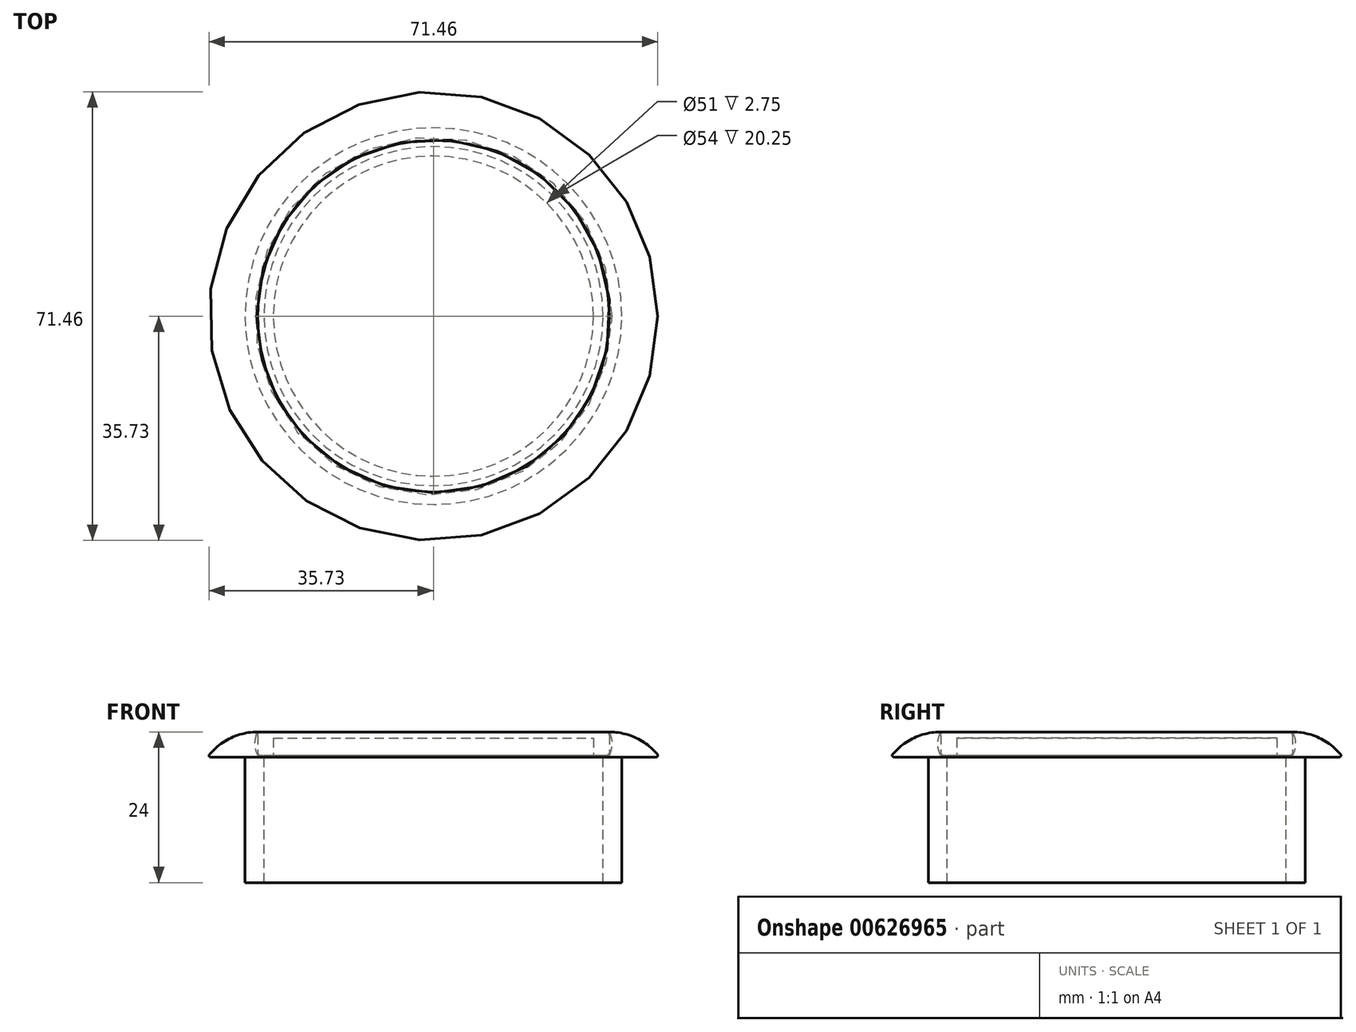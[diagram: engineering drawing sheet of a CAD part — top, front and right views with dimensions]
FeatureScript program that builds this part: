
annotation { "Feature Type Name" : "Feature", "Feature Type Description" : "" }
export const myFeature = defineFeature(function(context is Context, id is Id, definition is map)
    precondition{}
    {
        {
            var Q0;
            Q0=qCreatedBy(makeId("Top.planeOp"),FACE);
            var sketch = newSketch(context, id + "F0", { "sketchPlane" : qUnion([Q0])});
            skCircle(sketch, "E0", {"center": v(0, 0) * mm, "radius": 27 * mm});
            skCircle(sketch, "E1", {"center": v(0, 0) * mm, "radius": 30 * mm});
            skSolve(sketch);
        }
        {
            var Q0;
            Q0=makeQuery(id+"F0.imprint","IMPRINT",FACE,{"disambiguationData":[TD([[makeQuery(id+"F0.imprint","IMPRINT",EDGE,{"derivedFrom":sQuery(id+"F0.wireOp",EDGE,"E0")}),-1.0]])]});
            extrude(context, id + "F1", {"entities" : qUnion([Q0]), "oppositeDirection" : true, "depth" : 20 * mm, "offsetDistance" : 25 * mm});
        }
        {
            var Q0;
            Q0=qCreatedBy(makeId("Front.planeOp"),FACE);
            var sketch = newSketch(context, id + "F2", { "sketchPlane" : qUnion([Q0])});
            skPoint(sketch, "E2", {"position": v(-27, 0) * mm});
            skPoint(sketch, "E3", {"position": v(-30, 0) * mm});
            skLineSegment(sketch, "E4", {"start": v(-27, 0) * mm, "end": v(-27, 0.25) * mm});
            skLineSegment(sketch, "E5", {"start": v(-27, 0.25) * mm, "end": v(-28, 0.25) * mm});
            skLineSegment(sketch, "E6", {"start": v(-28, 0.25) * mm, "end": v(-28, 4) * mm});
            skLineSegment(sketch, "E7", {"start": v(-30, 0) * mm, "end": v(-36, 0) * mm});
            skLineSegment(sketch, "E8", {"start": v(-28, 4) * mm, "end": v(0, 4) * mm});
            skLineSegment(sketch, "E9", {"start": v(0, 4) * mm, "end": v(0, 0) * mm, "construction": true});
            skArc(sketch, "E10", {"start": v(-28, 4) * mm, "mid": v(-32.47, 2.94) * mm, "end": v(-36, 0) * mm});
            skLineSegment(sketch, "E11", {"start": v(-30, 0) * mm, "end": v(-27, 0) * mm});
            skArc(sketch, "E12", {"start": v(-28, 4) * mm, "mid": v(-28.47, 2.13) * mm, "end": v(-28, 0.25) * mm});
            skLineSegment(sketch, "E13", {"start": v(-27, 0.25) * mm, "end": v(0, 0.25) * mm});
            skLineSegment(sketch, "E14", {"start": v(0, 0.25) * mm, "end": v(0, 4) * mm});
            skSolve(sketch);
        }
        {
            var Q0;
            Q0=makeQuery(id+"F2.imprint","IMPRINT",FACE,{"disambiguationData":[TD([[makeQuery(id+"F2.imprint","IMPRINT",EDGE,{"derivedFrom":sQuery(id+"F2.wireOp",EDGE,"E4")}),1.0]])]});
            var Q1;
            Q1=sQuery(id+"F2.wireOp",EDGE,"E9");
            revolve(context, id + "F3", {"operationType" : NewBodyOperationType.ADD, "entities" : qUnion([Q0]), "axis" : qUnion([Q1]), "revolveType" : RevolveType.FULL});
        }
        {
            var Q0;
            Q0=makeQuery(id+"F3.opRevolve","SWEPT_EDGE",EDGE,{"disambiguationData":[OSD([sQuery(id+"F2.wireOp",EDGE,"E8"),sQuery(id+"F2.wireOp",EDGE,"E10"),sQuery(id+"F2.wireOp",EDGE,"E12")])]});
            var Q1;
            Q1=makeQuery(id+"F3.opRevolve","SWEPT_EDGE",EDGE,{"disambiguationData":[OSD([sQuery(id+"F2.wireOp",EDGE,"E7"),sQuery(id+"F2.wireOp",EDGE,"E10")])]});
            fillet(context, id + "F4", {"entities" : qUnion([Q0, Q1]), "radius" : 0.25 * mm, "tangentPropagation" : true, "allowEdgeOverflow" : false});
        }
        {
            var Q0;
            Q0=makeQuery(id+"F2.imprint","IMPRINT",FACE,{"disambiguationData":[TD([[makeQuery(id+"F2.imprint","IMPRINT",EDGE,{"derivedFrom":sQuery(id+"F2.wireOp",EDGE,"E5")}),-1.0]])]});
            var Q1;
            Q1=sQuery(id+"F2.wireOp",EDGE,"E14");
            revolve(context, id + "F5", {"entities" : qUnion([Q0]), "axis" : qUnion([Q1]), "revolveType" : RevolveType.FULL});
        }
        {
            var Q0;
            Q0=makeQuery(id+"F5.opRevolve","SWEPT_EDGE",EDGE,{"disambiguationData":[OSD([sQuery(id+"F2.wireOp",EDGE,"E8"),sQuery(id+"F2.wireOp",EDGE,"E10"),sQuery(id+"F2.wireOp",EDGE,"E12")])]});
            var Q1;
            Q1=makeQuery(id+"F5.opRevolve","SWEPT_EDGE",EDGE,{"disambiguationData":[OSD([sQuery(id+"F2.wireOp",EDGE,"E5"),sQuery(id+"F2.wireOp",EDGE,"E6"),sQuery(id+"F2.wireOp",EDGE,"E12")])]});
            fillet(context, id + "F6", {"entities" : qUnion([Q0, Q1]), "radius" : 0.5 * mm, "tangentPropagation" : true, "allowEdgeOverflow" : false});
        }
        {
            var Q0;
            Q0=makeQuery(id+"F5.opRevolve","SWEPT_FACE",FACE,{"disambiguationData":[OSD([sQuery(id+"F2.wireOp",EDGE,"E5"),sQuery(id+"F2.wireOp",EDGE,"E13")])]});
            var sketch = newSketch(context, id + "F7", { "sketchPlane" : qUnion([Q0])});
            skCircle(sketch, "E15", {"center": v(0, 0) * mm, "radius": 25.5 * mm});
            skSolve(sketch);
        }
        {
            var Q0;
            Q0=makeQuery(id+"F7.imprint","IMPRINT",FACE,{"disambiguationData":[TD([[makeQuery(id+"F7.imprint","IMPRINT",EDGE,{"derivedFrom":sQuery(id+"F7.wireOp",EDGE,"E15")}),1.0]])]});
            extrude(context, id + "F8", {"entities" : qUnion([Q0]), "operationType" : NewBodyOperationType.REMOVE, "oppositeDirection" : true, "depth" : 2.75 * mm, "offsetDistance" : 25 * mm});
        }
    });
